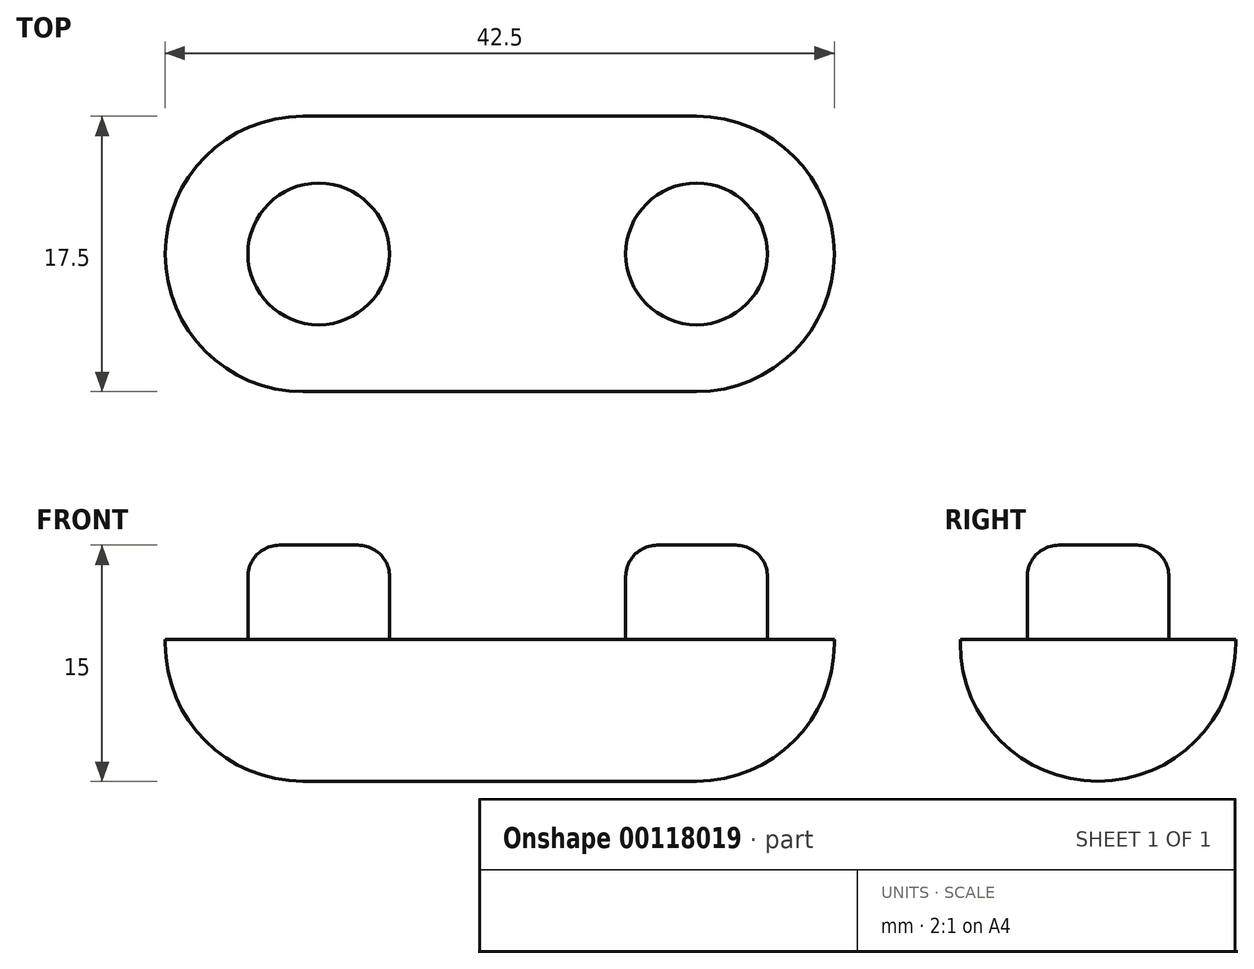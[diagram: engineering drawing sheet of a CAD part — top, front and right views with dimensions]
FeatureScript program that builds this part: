
annotation { "Feature Type Name" : "Feature", "Feature Type Description" : "" }
export const myFeature = defineFeature(function(context is Context, id is Id, definition is map)
    precondition{}
    {
        {
            var Q0;
            Q0=qCreatedBy(makeId("Top.planeOp"),FACE);
            var sketch = newSketch(context, id + "F0", { "sketchPlane" : qUnion([Q0])});
            skArc(sketch, "E0", {"start": v(-12.5, 8.75) * mm, "mid": v(-18.69, 6.19) * mm, "end": v(-21.25, 0) * mm});
            skArc(sketch, "E1", {"start": v(-21.25, 0) * mm, "mid": v(-18.69, -6.19) * mm, "end": v(-12.5, -8.75) * mm});
            skArc(sketch, "E2", {"start": v(12.5, 8.75) * mm, "mid": v(18.69, 6.19) * mm, "end": v(21.25, 0) * mm});
            skArc(sketch, "E3", {"start": v(21.25, 0) * mm, "mid": v(18.69, -6.19) * mm, "end": v(12.5, -8.75) * mm});
            skLineSegment(sketch, "E4", {"start": v(-12.5, 8.75) * mm, "end": v(12.5, 8.75) * mm});
            skLineSegment(sketch, "E5", {"start": v(12.5, -8.75) * mm, "end": v(-12.5, -8.75) * mm});
            skSolve(sketch);
        }
        {
            var Q0;
            Q0=makeQuery(id+"F0.imprint","IMPRINT",FACE,{"disambiguationData":[TD([[makeQuery(id+"F0.imprint","IMPRINT",EDGE,{"derivedFrom":sQuery(id+"F0.wireOp",EDGE,"E0")}),1.0]])]});
            extrude(context, id + "F1", {"entities" : qUnion([Q0]), "depth" : 9 * mm});
        }
        {
            var Q0;
            Q0=makeQuery(id+"F1.opExtrude","CAP_EDGE",EDGE,{"disambiguationData":[OSD([sQuery(id+"F0.wireOp",EDGE,"E2"),sQuery(id+"F0.wireOp",EDGE,"E3")])],"isStart":true});
            fillet(context, id + "F2", {"entities" : qUnion([Q0]), "radius" : 8.75 * mm, "tangentPropagation" : true, "allowEdgeOverflow" : false});
        }
        {
            var Q0;
            Q0=makeQuery(id+"F1.opExtrude","CAP_FACE",FACE,{"disambiguationData":[OSD([sQuery(id+"F0.wireOp",EDGE,"E0"),sQuery(id+"F0.wireOp",EDGE,"E1"),sQuery(id+"F0.wireOp",EDGE,"E2"),sQuery(id+"F0.wireOp",EDGE,"E3"),sQuery(id+"F0.wireOp",EDGE,"E4"),sQuery(id+"F0.wireOp",EDGE,"E5")])],"isStart":false});
            var sketch = newSketch(context, id + "F3", { "sketchPlane" : qUnion([Q0])});
            skCircle(sketch, "E6", {"center": v(-11.5, 0) * mm, "radius": 4.5 * mm});
            skCircle(sketch, "E7", {"center": v(12.5, 0) * mm, "radius": 4.5 * mm});
            skSolve(sketch);
        }
        {
            var Q0;
            Q0=makeQuery(id+"F3.imprint","IMPRINT",FACE,{"disambiguationData":[TD([[makeQuery(id+"F3.imprint","IMPRINT",EDGE,{"derivedFrom":sQuery(id+"F3.wireOp",EDGE,"E7")}),1.0]])]});
            var Q1;
            Q1=makeQuery(id+"F3.imprint","IMPRINT",FACE,{"disambiguationData":[TD([[makeQuery(id+"F3.imprint","IMPRINT",EDGE,{"derivedFrom":sQuery(id+"F3.wireOp",EDGE,"E6")}),1.0]])]});
            extrude(context, id + "F4", {"entities" : qUnion([Q0, Q1]), "operationType" : NewBodyOperationType.ADD, "depth" : 6 * mm});
        }
        {
            var Q0;
            Q0=makeQuery(id+"F4.opExtrude","CAP_EDGE",EDGE,{"disambiguationData":[OSD([sQuery(id+"F3.wireOp",EDGE,"E6")])],"isStart":false});
            var Q1;
            Q1=makeQuery(id+"F4.opExtrude","CAP_EDGE",EDGE,{"disambiguationData":[OSD([sQuery(id+"F3.wireOp",EDGE,"E7")])],"isStart":false});
            fillet(context, id + "F5", {"entities" : qUnion([Q0, Q1]), "radius" : 2 * mm, "tangentPropagation" : true, "allowEdgeOverflow" : false});
        }
    });
